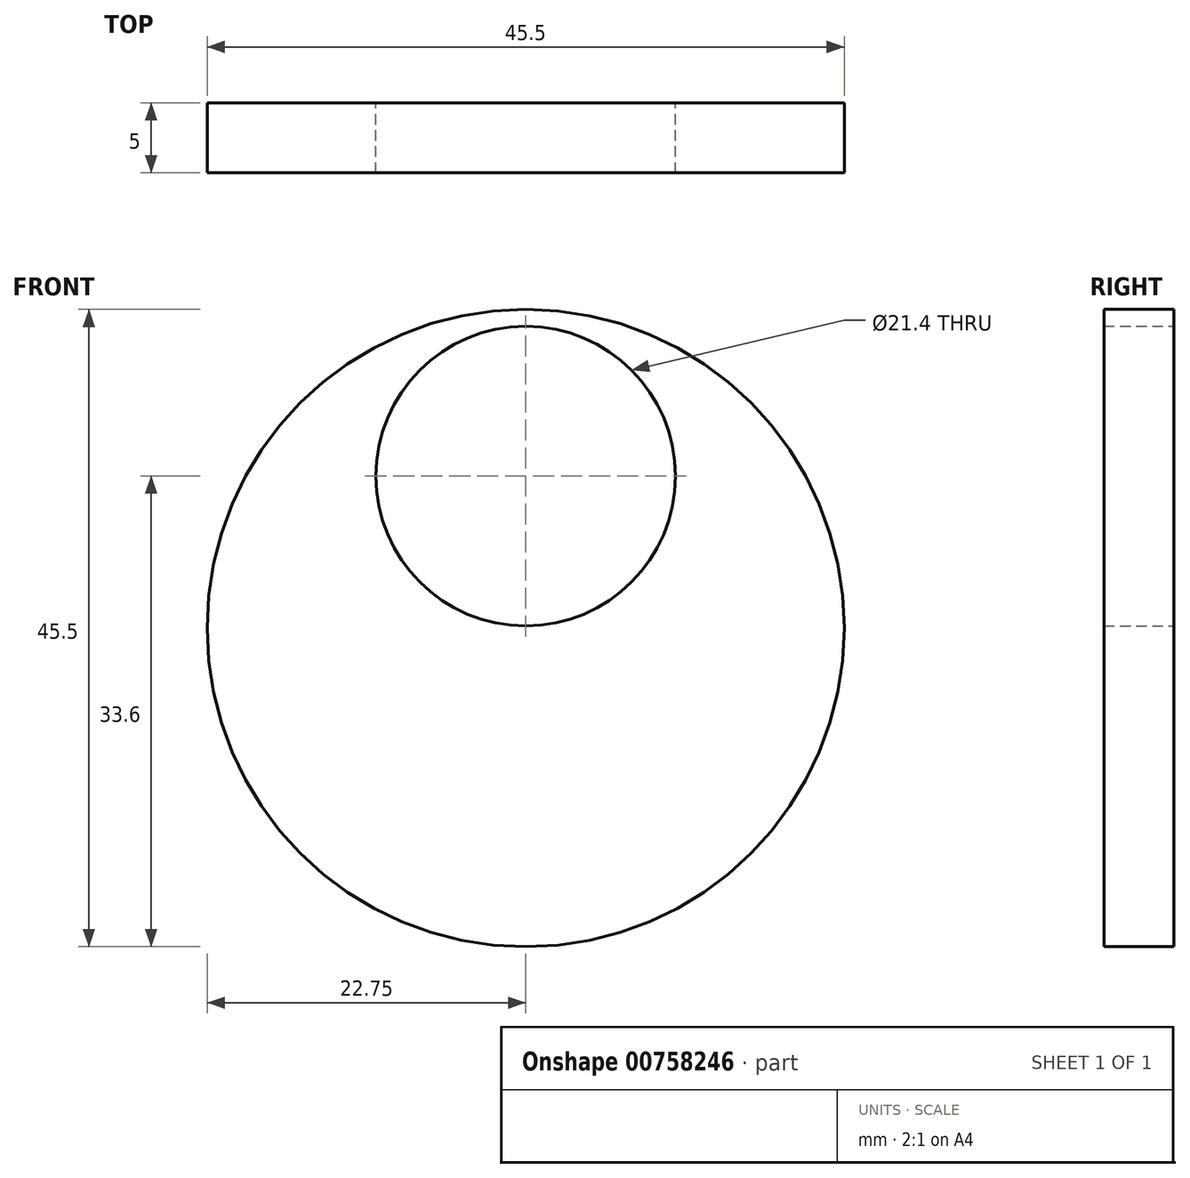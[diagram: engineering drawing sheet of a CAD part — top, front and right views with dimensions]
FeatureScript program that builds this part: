
annotation { "Feature Type Name" : "Feature", "Feature Type Description" : "" }
export const myFeature = defineFeature(function(context is Context, id is Id, definition is map)
    precondition{}
    {
        {
            var Q0;
            Q0=qCreatedBy(makeId("Front.planeOp"),FACE);
            var sketch = newSketch(context, id + "F0", { "sketchPlane" : qUnion([Q0])});
            skCircle(sketch, "E0", {"center": v(0, 0) * mm, "radius": 22.75 * mm});
            skCircle(sketch, "E1", {"center": v(0, 10.85) * mm, "radius": 10.7 * mm});
            skLineSegment(sketch, "E2", {"start": v(0, 22.75) * mm, "end": v(0, -22.75) * mm, "construction": true});
            skSolve(sketch);
        }
        {
            var Q0;
            Q0=makeQuery(id+"F0.imprint","IMPRINT",FACE,{"disambiguationData":[TD([[makeQuery(id+"F0.imprint","IMPRINT",EDGE,{"derivedFrom":sQuery(id+"F0.wireOp",EDGE,"E0")}),1.0]])]});
            extrude(context, id + "F1", {"entities" : qUnion([Q0]), "depth" : 5 * mm, "offsetDistance" : 25 * mm});
        }
    });
